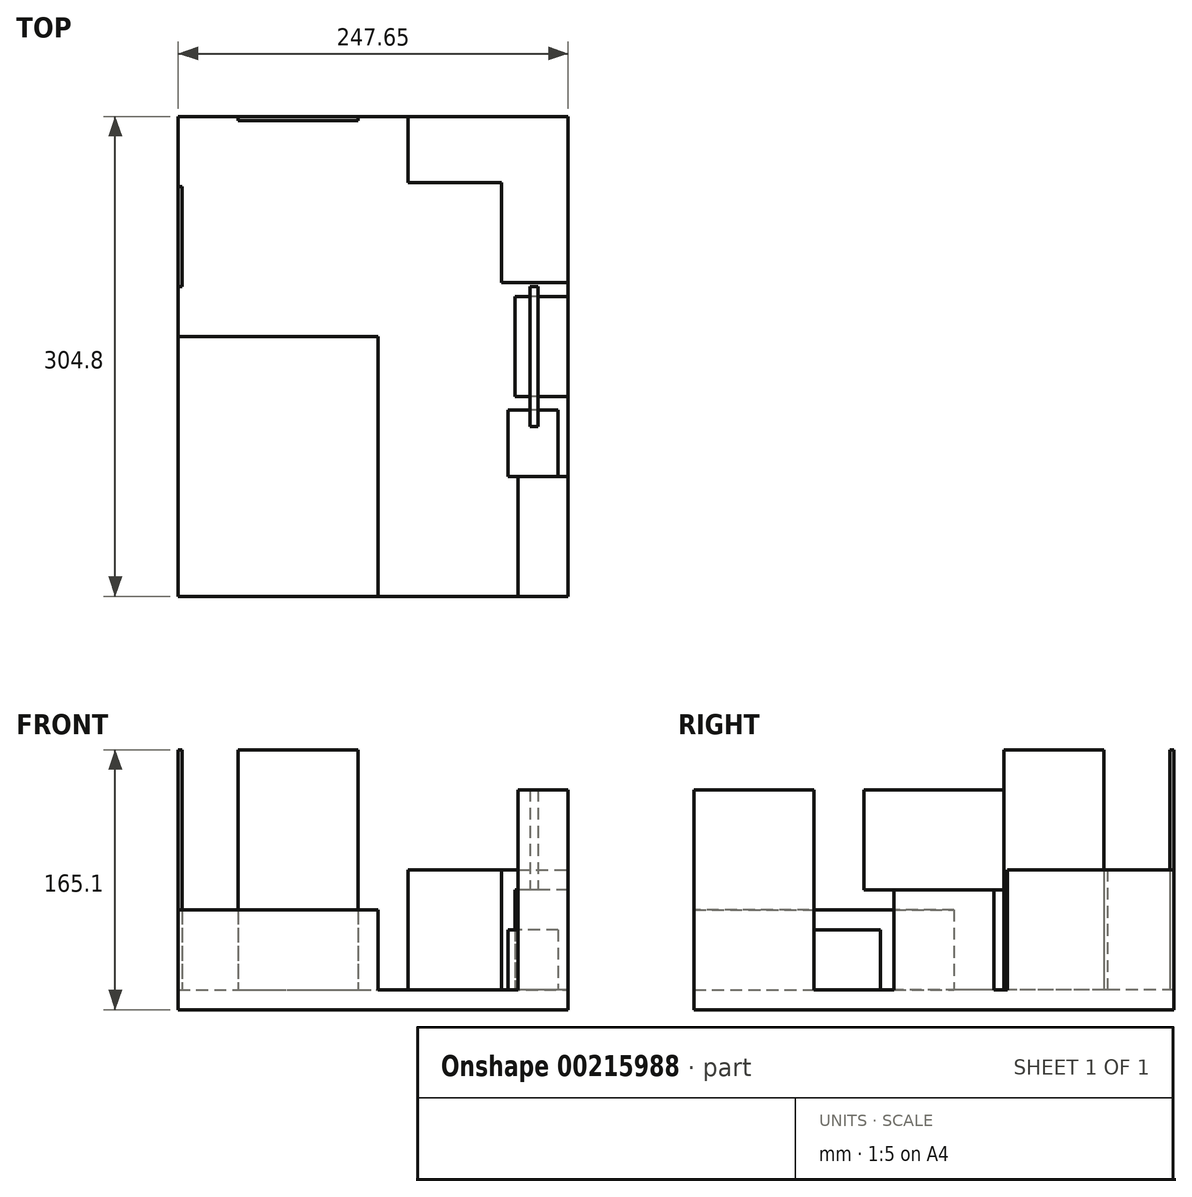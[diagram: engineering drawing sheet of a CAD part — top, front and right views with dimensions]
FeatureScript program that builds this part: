
annotation { "Feature Type Name" : "Feature", "Feature Type Description" : "" }
export const myFeature = defineFeature(function(context is Context, id is Id, definition is map)
    precondition{}
    {
        {
            var Q0;
            Q0=qCreatedBy(makeId("Top.planeOp"),FACE);
            var sketch = newSketch(context, id + "F0", { "sketchPlane" : qUnion([Q0])});
            skLineSegment(sketch, "E0.bottom", {"start": v(0, 0) * mm, "end": v(247.65, 0) * mm});
            skLineSegment(sketch, "E0.top", {"start": v(0, -304.8) * mm, "end": v(247.65, -304.8) * mm});
            skLineSegment(sketch, "E0.left", {"start": v(0, 0) * mm, "end": v(0, -304.8) * mm});
            skLineSegment(sketch, "E0.right", {"start": v(247.65, 0) * mm, "end": v(247.65, -304.8) * mm});
            skSolve(sketch);
        }
        {
            var Q0;
            Q0 = qSketchRegion(id + "F0", true);
            extrude(context, id + "F1", {"entities" : qUnion([Q0]), "depth" : 12.7 * mm});
        }
        {
            var Q0;
            Q0=makeQuery(id+"F1.opExtrude","CAP_FACE",FACE,{"disambiguationData":[OSD([sQuery(id+"F0.wireOp",EDGE,"E0.bottom"),sQuery(id+"F0.wireOp",EDGE,"E0.top"),sQuery(id+"F0.wireOp",EDGE,"E0.left"),sQuery(id+"F0.wireOp",EDGE,"E0.right")])],"isStart":false});
            var sketch = newSketch(context, id + "F2", { "sketchPlane" : qUnion([Q0])});
            skLineSegment(sketch, "E1.bottom", {"start": v(0, -44.45) * mm, "end": v(2.54, -44.45) * mm});
            skLineSegment(sketch, "E1.top", {"start": v(0, -107.95) * mm, "end": v(2.54, -107.95) * mm});
            skLineSegment(sketch, "E1.left", {"start": v(0, -44.45) * mm, "end": v(0, -107.95) * mm});
            skLineSegment(sketch, "E1.right", {"start": v(2.54, -44.45) * mm, "end": v(2.54, -107.95) * mm});
            skSolve(sketch);
        }
        {
            var Q0;
            Q0 = qSketchRegion(id + "F2", true);
            extrude(context, id + "F3", {"entities" : qUnion([Q0]), "operationType" : NewBodyOperationType.ADD, "depth" : 152.4 * mm});
        }
        {
            var Q0;
            Q0=makeQuery(id+"F1.opExtrude","CAP_FACE",FACE,{"disambiguationData":[OSD([sQuery(id+"F0.wireOp",EDGE,"E0.bottom"),sQuery(id+"F0.wireOp",EDGE,"E0.top"),sQuery(id+"F0.wireOp",EDGE,"E0.left"),sQuery(id+"F0.wireOp",EDGE,"E0.right")])],"isStart":false});
            var sketch = newSketch(context, id + "F4", { "sketchPlane" : qUnion([Q0])});
            skLineSegment(sketch, "E2.bottom", {"start": v(38.1, 0) * mm, "end": v(114.3, 0) * mm});
            skLineSegment(sketch, "E2.top", {"start": v(38.1, -2.54) * mm, "end": v(114.3, -2.54) * mm});
            skLineSegment(sketch, "E2.left", {"start": v(38.1, 0) * mm, "end": v(38.1, -2.54) * mm});
            skLineSegment(sketch, "E2.right", {"start": v(114.3, 0) * mm, "end": v(114.3, -2.54) * mm});
            skSolve(sketch);
        }
        {
            var Q0;
            Q0 = qSketchRegion(id + "F4", true);
            extrude(context, id + "F5", {"entities" : qUnion([Q0]), "operationType" : NewBodyOperationType.ADD, "depth" : 152.4 * mm});
        }
        {
            var Q0;
            Q0=makeQuery(id+"F1.opExtrude","CAP_FACE",FACE,{"disambiguationData":[OSD([sQuery(id+"F0.wireOp",EDGE,"E0.bottom"),sQuery(id+"F0.wireOp",EDGE,"E0.top"),sQuery(id+"F0.wireOp",EDGE,"E0.left"),sQuery(id+"F0.wireOp",EDGE,"E0.right")])],"isStart":false});
            var sketch = newSketch(context, id + "F6", { "sketchPlane" : qUnion([Q0])});
            skLineSegment(sketch, "E3.bottom", {"start": v(247.65, 0) * mm, "end": v(146.05, 0) * mm});
            skLineSegment(sketch, "E3.top", {"start": v(247.65, -42.16) * mm, "end": v(146.05, -42.16) * mm});
            skLineSegment(sketch, "E3.left", {"start": v(247.65, 0) * mm, "end": v(247.65, -42.16) * mm});
            skLineSegment(sketch, "E3.right", {"start": v(146.05, 0) * mm, "end": v(146.05, -42.16) * mm});
            skLineSegment(sketch, "E4.bottom", {"start": v(205.49, -42.16) * mm, "end": v(247.65, -42.16) * mm});
            skLineSegment(sketch, "E4.top", {"start": v(205.49, -105.66) * mm, "end": v(247.65, -105.66) * mm});
            skLineSegment(sketch, "E4.left", {"start": v(205.49, -42.16) * mm, "end": v(205.49, -105.66) * mm});
            skLineSegment(sketch, "E4.right", {"start": v(247.65, -42.16) * mm, "end": v(247.65, -105.66) * mm});
            skSolve(sketch);
        }
        {
            var Q0;
            Q0 = qSketchRegion(id + "F6", true);
            extrude(context, id + "F7", {"entities" : qUnion([Q0]), "operationType" : NewBodyOperationType.ADD, "depth" : 76.2 * mm});
        }
        {
            var Q0;
            Q0=makeQuery(id+"F1.opExtrude","CAP_FACE",FACE,{"disambiguationData":[OSD([sQuery(id+"F0.wireOp",EDGE,"E0.bottom"),sQuery(id+"F0.wireOp",EDGE,"E0.top"),sQuery(id+"F0.wireOp",EDGE,"E0.left"),sQuery(id+"F0.wireOp",EDGE,"E0.right")])],"isStart":false});
            var sketch = newSketch(context, id + "F8", { "sketchPlane" : qUnion([Q0])});
            skLineSegment(sketch, "E5.bottom", {"start": v(247.65, -114.3) * mm, "end": v(213.87, -114.3) * mm});
            skLineSegment(sketch, "E5.top", {"start": v(247.65, -177.8) * mm, "end": v(213.87, -177.8) * mm});
            skLineSegment(sketch, "E5.left", {"start": v(247.65, -114.3) * mm, "end": v(247.65, -177.8) * mm});
            skLineSegment(sketch, "E5.right", {"start": v(213.87, -114.3) * mm, "end": v(213.87, -177.8) * mm});
            skSolve(sketch);
        }
        {
            var Q0;
            Q0 = qSketchRegion(id + "F8", true);
            extrude(context, id + "F9", {"entities" : qUnion([Q0]), "operationType" : NewBodyOperationType.ADD, "depth" : 63.5 * mm});
        }
        {
            var Q0;
            Q0=makeQuery(id+"F9.opExtrude","CAP_FACE",FACE,{"disambiguationData":[OSD([sQuery(id+"F8.wireOp",EDGE,"E5.bottom"),sQuery(id+"F8.wireOp",EDGE,"E5.top"),sQuery(id+"F8.wireOp",EDGE,"E5.left"),sQuery(id+"F8.wireOp",EDGE,"E5.right")])],"isStart":false});
            var sketch = newSketch(context, id + "F10", { "sketchPlane" : qUnion([Q0])});
            skLineSegment(sketch, "E6.bottom", {"start": v(223.52, -107.95) * mm, "end": v(228.6, -107.95) * mm});
            skLineSegment(sketch, "E6.top", {"start": v(223.52, -196.85) * mm, "end": v(228.6, -196.85) * mm});
            skLineSegment(sketch, "E6.left", {"start": v(223.52, -107.95) * mm, "end": v(223.52, -196.85) * mm});
            skLineSegment(sketch, "E6.right", {"start": v(228.6, -107.95) * mm, "end": v(228.6, -196.85) * mm});
            skSolve(sketch);
        }
        {
            var Q0;
            Q0 = qSketchRegion(id + "F10", true);
            extrude(context, id + "F11", {"entities" : qUnion([Q0]), "operationType" : NewBodyOperationType.ADD, "depth" : 63.5 * mm});
        }
        {
            var Q0;
            Q0=makeQuery(id+"F1.opExtrude","CAP_FACE",FACE,{"disambiguationData":[OSD([sQuery(id+"F0.wireOp",EDGE,"E0.bottom"),sQuery(id+"F0.wireOp",EDGE,"E0.top"),sQuery(id+"F0.wireOp",EDGE,"E0.left"),sQuery(id+"F0.wireOp",EDGE,"E0.right")])],"isStart":false});
            var sketch = newSketch(context, id + "F12", { "sketchPlane" : qUnion([Q0])});
            skLineSegment(sketch, "E7.bottom", {"start": v(247.65, -304.8) * mm, "end": v(215.9, -304.8) * mm});
            skLineSegment(sketch, "E7.top", {"start": v(247.65, -228.6) * mm, "end": v(215.9, -228.6) * mm});
            skLineSegment(sketch, "E7.left", {"start": v(247.65, -304.8) * mm, "end": v(247.65, -228.6) * mm});
            skLineSegment(sketch, "E7.right", {"start": v(215.9, -304.8) * mm, "end": v(215.9, -228.6) * mm});
            skSolve(sketch);
        }
        {
            var Q0;
            Q0 = qSketchRegion(id + "F12", true);
            extrude(context, id + "F13", {"entities" : qUnion([Q0]), "operationType" : NewBodyOperationType.ADD, "depth" : 127 * mm});
        }
        {
            var Q0;
            Q0=makeQuery(id+"F1.opExtrude","CAP_FACE",FACE,{"disambiguationData":[OSD([sQuery(id+"F0.wireOp",EDGE,"E0.bottom"),sQuery(id+"F0.wireOp",EDGE,"E0.top"),sQuery(id+"F0.wireOp",EDGE,"E0.left"),sQuery(id+"F0.wireOp",EDGE,"E0.right")])],"isStart":false});
            var sketch = newSketch(context, id + "F14", { "sketchPlane" : qUnion([Q0])});
            skLineSegment(sketch, "E8.bottom", {"start": v(241.3, -228.6) * mm, "end": v(209.55, -228.6) * mm});
            skLineSegment(sketch, "E8.top", {"start": v(241.3, -186.44) * mm, "end": v(209.55, -186.44) * mm});
            skLineSegment(sketch, "E8.left", {"start": v(241.3, -228.6) * mm, "end": v(241.3, -186.44) * mm});
            skLineSegment(sketch, "E8.right", {"start": v(209.55, -228.6) * mm, "end": v(209.55, -186.44) * mm});
            skSolve(sketch);
        }
        {
            var Q0;
            Q0 = qSketchRegion(id + "F14", true);
            extrude(context, id + "F15", {"entities" : qUnion([Q0]), "operationType" : NewBodyOperationType.ADD, "depth" : 38.1 * mm});
        }
        {
            var Q0;
            Q0=makeQuery(id+"F1.opExtrude","CAP_FACE",FACE,{"disambiguationData":[OSD([sQuery(id+"F0.wireOp",EDGE,"E0.bottom"),sQuery(id+"F0.wireOp",EDGE,"E0.top"),sQuery(id+"F0.wireOp",EDGE,"E0.left"),sQuery(id+"F0.wireOp",EDGE,"E0.right")])],"isStart":false});
            var sketch = newSketch(context, id + "F16", { "sketchPlane" : qUnion([Q0])});
            skLineSegment(sketch, "E9.bottom", {"start": v(0, -304.8) * mm, "end": v(127, -304.8) * mm});
            skLineSegment(sketch, "E9.top", {"start": v(0, -139.7) * mm, "end": v(127, -139.7) * mm});
            skLineSegment(sketch, "E9.left", {"start": v(0, -304.8) * mm, "end": v(0, -139.7) * mm});
            skLineSegment(sketch, "E9.right", {"start": v(127, -304.8) * mm, "end": v(127, -139.7) * mm});
            skSolve(sketch);
        }
        {
            var Q0;
            Q0 = qSketchRegion(id + "F16", true);
            extrude(context, id + "F17", {"entities" : qUnion([Q0]), "operationType" : NewBodyOperationType.ADD, "depth" : 50.8 * mm});
        }
    });
